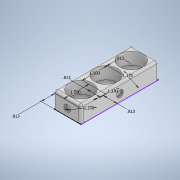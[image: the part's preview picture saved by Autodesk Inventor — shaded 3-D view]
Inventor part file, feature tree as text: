
AUTODESK INVENTOR PART (.ipt)
format: ipt  version: 2021 (Build 250183000, 183)  size: 346,624 bytes
history: native  units: in
note: dims shown in document units (in); Inventor stores cm internally (conversion verified against a paired STEP export)
features: extrude x6, sketch x5, fillet x1
ambient origin geometry x8: Origin, YZ Plane, XZ Plane, XY Plane, X Axis, Y Axis, Z Axis, Center Point
bodies: Solid1 (feature_tree)
feature tree (12):
  sketch  "Sketch1"  dims[d0=1.37in d1=1.37in]
  extrude  "Extrusion1"  Depth=1.37in
  extrude  "Extrusion2"  Depth=1.5in
  fillet  "Fillet1"  Radius=1.5in
  extrude  "Extrusion4"  Depth=0.813in
  extrude  "Extrusion5"  Depth=0.813in
  extrude  "Extrusion6"  Depth=0.25in TaperAngle=0.0deg
  extrude  "Extrusion7"  Depth=0.125in
  sketch  "Sketch3"  dims[d2=1.5in d3=1.37in d4=1.5in]
  sketch  "Sketch4"  dims[d5=0.813in d6=0.813in]
  sketch  "Sketch5"  dims[d7=0.813in d8=0.813in]
  sketch  "Sketch6"  dims[d9=0.9843in d10=0.0in d11=0.25in d12=0.0in d13=0.125in d19=0.3937in d20=2.188in d21=0.4295in d22=0.1181in d23=0.0in d24=0.3937in d25=0.688in d26=0.4295in d27=0.1181in d28=0.0in d29=0.3937in d30=0.1181in d31=0.0in d32=0.1181in d33=0.0in]
